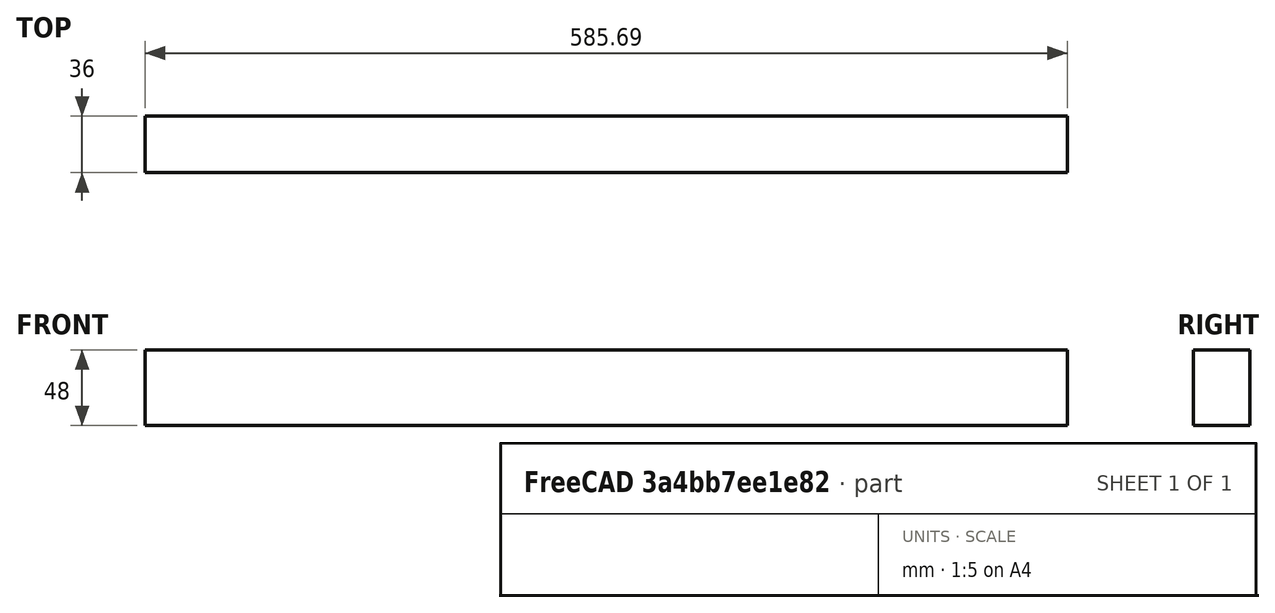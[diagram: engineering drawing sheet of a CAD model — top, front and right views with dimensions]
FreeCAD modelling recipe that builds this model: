
FCSTD DOCUMENT  (FreeCAD 0.19R24267 (Git))
Label: windowFrameHeight
License: Creative Commons Attribution-ShareAlike
LicenseURL: http://creativecommons.org/licenses/by-sa/4.0/
objects: Sketcher::SketchObject×1, Part::Extrusion×1
note: 2 computed .brp shape members not serialized (recipe doc carries the construction recipe); baked Part::Feature solids carry a one-line shape summary decoded from their .brp
EXTERNAL_REF file=Main.FCStd obj=Spreadsheet

FEATURE [Sketcher::SketchObject] Sketch
  FullyConstrained = true
  expr: Constraints[8] = Main#<<params>>.structuralWoodHeight
  expr: Constraints[9] = Main#<<params>>.windowHeight + 20
  sketch-geometry (4):
    g0: LineSegment StartX=0 StartY=0 StartZ=0 EndX=2.2e-15 EndY=36 EndZ=0
    g1: LineSegment StartX=2.2e-15 StartY=36 StartZ=0 EndX=585.685 EndY=36 EndZ=0
    g2: LineSegment StartX=585.685 StartY=36 StartZ=0 EndX=585.685 EndY=0 EndZ=0
    g3: LineSegment StartX=585.685 StartY=0 StartZ=0 EndX=0 EndY=0 EndZ=0
  constraints (11):
    c: Coincident(g-1,g0)
    c: Coincident(g0,g1)
    c: Horizontal(g1)
    c: Coincident(g1,g2)
    c: PointOnObject(g2,g-1)
    c: Coincident(g2,g3)
    c: Coincident(g3,g0)
    c: Angle(g3,g0) = 1.5708
    c: DistanceY(g0,g0) = 36
    c: Distance(g3) = 585.685
    c: Equal(g0,g2)
FEATURE [Part::Extrusion] Extrude
  Base = -> Sketch
  Dir = (0,0,1)
  DirMode = 2
  FaceMakerClass = Part::FaceMakerBullseye
  LengthFwd = 48
  LengthRev = 0
  Solid = true
  Symmetric = false
  expr: LengthFwd = Main#<<params>>.structuralWoodWidth
